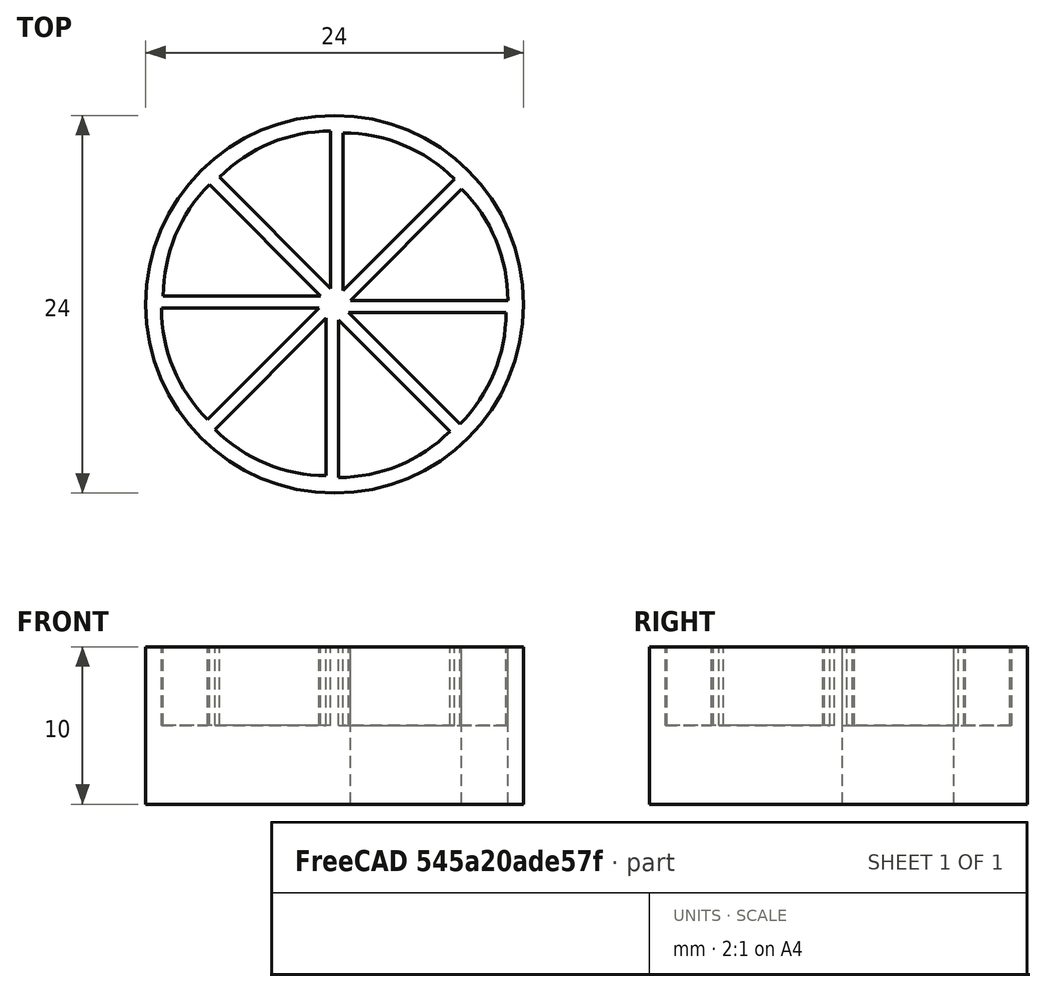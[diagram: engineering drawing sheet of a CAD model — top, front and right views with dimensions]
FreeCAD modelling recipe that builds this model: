
FCSTD DOCUMENT  (FreeCAD 1.0R39319 (Git))
Label: ojt1_t11r02_trivial
License: All rights reserved
LicenseURL: https://en.wikipedia.org/wiki/All_rights_reserved
objects: Part::Cylinder×2, Part::FeaturePython×1, Part::Cut×1
note: 3 computed .brp shape members not serialized (recipe doc carries the construction recipe); baked Part::Feature solids carry a one-line shape summary decoded from their .brp

FEATURE [Part::Cylinder] Cylinder  label="Cilindre"
  Angle = 360
  AttacherType = Attacher::AttachEngine3D
  FirstAngle = 0
  Height = 10
  Radius = 12
  SecondAngle = 0
FEATURE [Part::Cylinder] Cylinder001  label="Cilindre001"
  Angle = 45
  AttacherType = Attacher::AttachEngine3D
  FirstAngle = 0
  Height = 10
  Placement = pos=(1,0.25,0) rot=(0,0,1;0rad)
  Radius = 10
  SecondAngle = 0
FEATURE [Part::FeaturePython] Array  # Draft array (typed FeaturePython)
  AlwaysSyncPlacement = false
  Angle = 360
  ArrayType = 1
  Axis = (0,0,1)
  Base = -> Cylinder001
  Center = (0,0,0)
  Count = 8
  ExpandArray = false
  Fuse = false
  IntervalAxis = (0,0,0)
  IntervalX = (100,0,0)
  IntervalY = (0,100,0)
  IntervalZ = (0,0,100)
  NumberCircles = 3
  NumberPolar = 8
  NumberX = 2
  NumberY = 2
  NumberZ = 1
  Placement = pos=(0,0,5) rot=(0,0,1;0rad)
  PlacementList = 8 placements: [(1,0.25,0),(0.53033,0.883883,0),(-0.25,1,0),(-0.883883,0.53033,0),(-1,-0.25,0),(-0.53033,-0.883883,0),(0.25,-1,0),(0.883883,-0.53033,0)]
  RadialDistance = 50
  ScaleList = (8) [(1,1,1),(1,1,1),(1,1,1),(1,1,1),(1,1,1),(1,1,1),(1,1,1),(1,1,1)]
  Symmetry = 1
  TangentialDistance = 25
FEATURE [Part::Cut] Cut
  Base = -> Cylinder
  Refine = true
  Tool = -> Array
